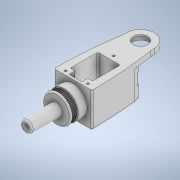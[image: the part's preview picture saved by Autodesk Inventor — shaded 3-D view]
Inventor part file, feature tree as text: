
AUTODESK INVENTOR PART (.ipt)
format: ipt  version: 2021 (Build 250183000, 183)  size: 2,227,200 bytes
history: native  units: mm
features: sketch x36, extrude x35, fillet x11, other x1
ambient origin geometry x8: Origin, YZ Plane, XZ Plane, XY Plane, X Axis, Y Axis, Z Axis, Center Point
bodies: Body1 (feature_tree)
feature tree (83):
  other  "Bryła1"
  extrude  "Wyciągnięcie proste1"  Depth=5.7mm TaperAngle=0.0deg
  extrude  "Wyciągnięcie proste2"  Depth=18.95mm
  sketch  "Szkic7"
  extrude  "Wyciągnięcie proste3"  Depth=1.25mm TaperAngle=0.0deg
  extrude  "Wyciągnięcie proste4"  Depth=34.0mm
  extrude  "Wyciągnięcie proste7"  Depth=26.0mm TaperAngle=0.0deg
  extrude  "Wyciągnięcie proste8"  TaperAngle=0.0deg  [1 undecoded]
  fillet  "Zaokrąglenie1"  Radius=22.5mm
  extrude  "Wyciągnięcie proste9"  Depth=22.1mm
  sketch  "Szkic20"
  extrude  "Wyciągnięcie proste10"  Depth=22.1mm
  sketch  "Szkic22"
  extrude  "Wyciągnięcie proste11"  Depth=3.0mm TaperAngle=0.0deg
  sketch  "Szkic26"
  extrude  "Wyciągnięcie proste13"  Depth=1.0mm
  fillet  "Zaokrąglenie2"  Radius=1.0mm
  fillet  "Zaokrąglenie3"  Radius=30.5mm
  sketch  "Szkic33"
  extrude  "Wyciągnięcie proste14"  Depth=10.0mm TaperAngle=0.0deg
  fillet  "Zaokrąglenie4"  Radius=2.5mm
  fillet  "Zaokrąglenie5"  Radius=29.0mm
  extrude  "Wyciągnięcie proste17"  Depth=2.0mm
  extrude  "Wyciągnięcie proste19"  Depth=2.0mm
  extrude  "Wyciągnięcie proste20"  Depth=2.0mm
  extrude  "Wyciągnięcie proste21"  Depth=2.0mm
  extrude  "Wyciągnięcie proste22"  Depth=32.95mm TaperAngle=0.0deg
  extrude  "Wyciągnięcie proste24"  Depth=16.475mm TaperAngle=0.0deg
  fillet  "Zaokrąglenie8"  Radius=19.5mm
  fillet  "Zaokrąglenie9"  Radius=9.75mm
  fillet  "Zaokrąglenie10"  Radius=9.75mm
  sketch  "Szkic58"
  extrude  "Wyciągnięcie proste27"  Depth=6.95mm TaperAngle=0.0deg
  sketch  "Szkic65"
  extrude  "Wyciągnięcie proste28"  Depth=550.0mm
  extrude  "Wyciągnięcie proste29"  Depth=15.0mm
  extrude  "Wyciągnięcie proste30"  Depth=6.95mm TaperAngle=0.0deg
  extrude  "Wyciągnięcie proste31"  Depth=550.0mm
  extrude  "Wyciągnięcie proste32"  Depth=15.0mm
  extrude  "Wyciągnięcie proste33"  Depth=2.0mm TaperAngle=0.0deg
  extrude  "Wyciągnięcie proste34"  Depth=10.0mm TaperAngle=0.0deg
  fillet  "Zaokrąglenie12"  Radius=37.0mm
  sketch  "Szkic78"
  extrude  "Wyciągnięcie proste37"  Depth=11.5mm TaperAngle=0.0deg
  extrude  "Wyciągnięcie proste38"  Depth=8.0mm TaperAngle=0.0deg
  fillet  "Zaokrąglenie13"  Radius=2.0mm
  extrude  "Wyciągnięcie proste40"  Depth=15.0mm TaperAngle=0.0deg
  extrude  "Wyciągnięcie proste41"  Depth=1.0mm
  extrude  "Wyciągnięcie proste42"  Depth=2.0mm
  extrude  "Wyciągnięcie proste43"  Depth=2.0mm
  fillet  "Zaokrąglenie14"  Radius=1.9mm
  extrude  "Wyciągnięcie proste44"  Depth=1.9mm
  extrude  "Wyciągnięcie proste45"  Depth=6.5mm
  extrude  "Wyciągnięcie proste48"  Depth=1.9mm
  extrude  "Wyciągnięcie proste49"  Depth=2.0mm
  sketch  "Szkic1"
  sketch  "Szkic2"
  sketch  "Szkic13"
  sketch  "Szkic15"
  sketch  "Szkic19"
  sketch  "Szkic23"
  sketch  "Szkic41"
  sketch  "Szkic42"
  sketch  "Szkic44"
  sketch  "Szkic45"
  sketch  "Szkic47"
  sketch  "Szkic51"
  sketch  "Szkic64"
  sketch  "Szkic67"
  sketch  "Szkic68"
  sketch  "Szkic69"
  sketch  "Szkic70"
  sketch  "Szkic71"
  sketch  "Szkic74"
  sketch  "Szkic81"
  sketch  "Szkic92"
  sketch  "Szkic93"
  sketch  "Szkic95"
  sketch  "Szkic97"
  sketch  "Szkic99"
  sketch  "Szkic106"
  sketch  "Szkic109"
  sketch  "Szkic110"
note: 1 required parameter value undecoded (feature->parameter linkage not recoverable at this tier; creation-order binding heuristic only, values carry confidence <= 0.55)
